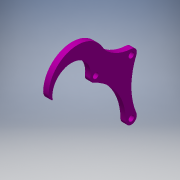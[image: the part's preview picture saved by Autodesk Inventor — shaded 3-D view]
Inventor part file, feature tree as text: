
AUTODESK INVENTOR PART (.ipt)
format: ipt  version: 2017 SP1 (Build 210196100, 196)  size: 147,968 bytes
history: native  units: in
note: dims shown in document units (in); Inventor stores cm internally (conversion verified against a paired STEP export)
features: extrude x1, fillet x1, sketch x1
ambient origin geometry x8: Origin, YZ Plane, XZ Plane, XY Plane, X Axis, Y Axis, Z Axis, Center Point
bodies: Solid1 (feature_tree)
feature tree (3):
  extrude  "Extrusion1"  Depth=0.02in
  fillet  "Fillet1"  Radius=0.25in
  sketch  "Sketch1"  dims[d0=2.5in d1=1.625in d2=0.25in d4=0.25in d6=1.75in d7=1.25in d8=0.1875in d9=0.375in d10=0.1875in d12=0.75in d13=0.75in d14=0.25in d15=0.0in d16=1.0in d17=0.02in d19=0.3846in]
